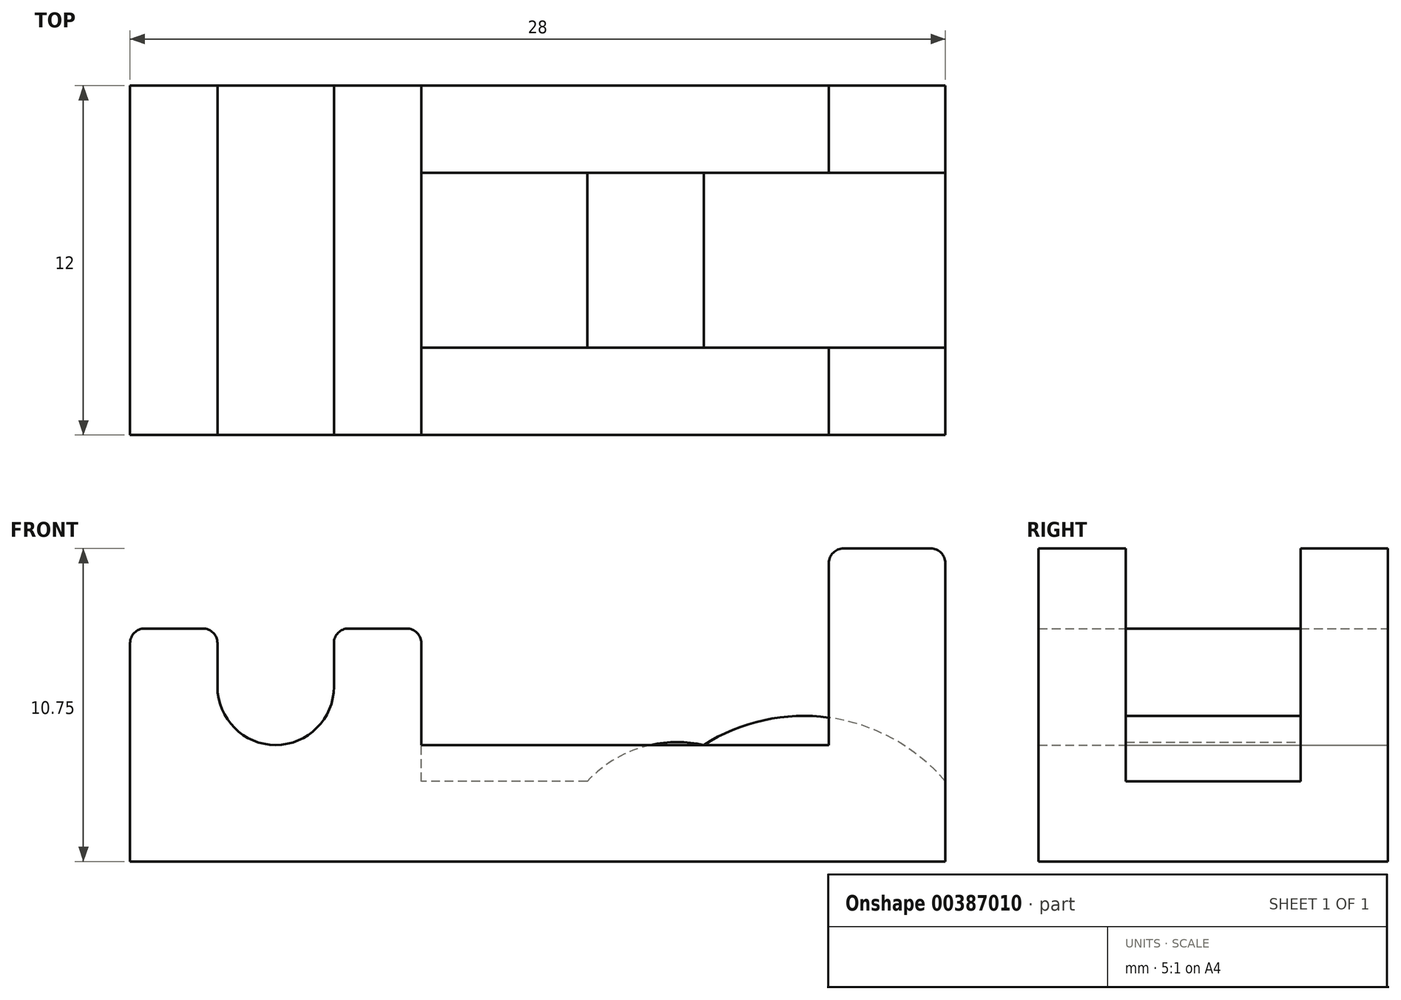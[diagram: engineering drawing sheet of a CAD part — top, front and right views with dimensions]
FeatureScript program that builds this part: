
annotation { "Feature Type Name" : "Feature", "Feature Type Description" : "" }
export const myFeature = defineFeature(function(context is Context, id is Id, definition is map)
    precondition{}
    {
        {
            var Q0;
            Q0=qCreatedBy(makeId("Front.planeOp"),FACE);
            var sketch = newSketch(context, id + "F0", { "sketchPlane" : qUnion([Q0])});
            skLineSegment(sketch, "E0", {"start": v(0, 0) * mm, "end": v(-28, 0) * mm});
            skLineSegment(sketch, "E1", {"start": v(0, 0) * mm, "end": v(0, 10.75) * mm});
            skLineSegment(sketch, "E2", {"start": v(0, 10.75) * mm, "end": v(-4, 10.75) * mm});
            skLineSegment(sketch, "E3", {"start": v(-4, 10.75) * mm, "end": v(-4, 4) * mm});
            skLineSegment(sketch, "E4", {"start": v(-4, 4) * mm, "end": v(-18, 4) * mm});
            skLineSegment(sketch, "E5", {"start": v(-28, 0) * mm, "end": v(-28, 8) * mm});
            skLineSegment(sketch, "E6", {"start": v(-25, 8) * mm, "end": v(-25, 6) * mm});
            skLineSegment(sketch, "E7", {"start": v(-21, 6) * mm, "end": v(-21, 8) * mm});
            skLineSegment(sketch, "E8", {"start": v(-18, 4) * mm, "end": v(-18, 8) * mm});
            skArc(sketch, "E9", {"start": v(-25, 6) * mm, "mid": v(-23, 4) * mm, "end": v(-21, 6) * mm});
            skLineSegment(sketch, "E10", {"start": v(-25, 8) * mm, "end": v(-28, 8) * mm});
            skLineSegment(sketch, "E11", {"start": v(-18, 8) * mm, "end": v(-21, 8) * mm});
            skSolve(sketch);
        }
        {
            var Q0;
            Q0=makeQuery(id+"F0.imprint","IMPRINT",FACE,{"disambiguationData":[TD([[makeQuery(id+"F0.imprint","IMPRINT",EDGE,{"derivedFrom":sQuery(id+"F0.wireOp",EDGE,"E0")}),-1.0]])]});
            extrude(context, id + "F1", {"entities" : qUnion([Q0]), "endBound" : BoundingType.SYMMETRIC, "depth" : 12 * mm});
        }
        {
            var Q0;
            Q0=makeQuery(id+"F1.opExtrude","SWEPT_FACE",FACE,{"disambiguationData":[OSD([sQuery(id+"F0.wireOp",EDGE,"E2")])]});
            var sketch = newSketch(context, id + "F2", { "sketchPlane" : qUnion([Q0])});
            skLineSegment(sketch, "E12.0", {"start": v(0, -6) * mm, "end": v(0, 6) * mm, "construction": true});
            skLineSegment(sketch, "E13.0", {"start": v(-18, -6) * mm, "end": v(-18, 6) * mm, "construction": true});
            skLineSegment(sketch, "E14.bottom", {"start": v(0, 3) * mm, "end": v(-18, 3) * mm});
            skLineSegment(sketch, "E14.top", {"start": v(0, -3) * mm, "end": v(-18, -3) * mm});
            skLineSegment(sketch, "E14.left", {"start": v(0, 3) * mm, "end": v(0, -3) * mm});
            skLineSegment(sketch, "E14.right", {"start": v(-18, 3) * mm, "end": v(-18, -3) * mm});
            skSolve(sketch);
        }
        {
            var Q0;
            {var subQ0=sQuery(id+"F2.wireOp",EDGE,"E14.right");Q0=makeQuery(id+"F2.imprint","IMPRINT",FACE,{"disambiguationData":[TD([[makeQuery(id+"F2.imprint","IMPRINT",EDGE,{"derivedFrom":subQ0}),1.0]])]});}
            var Q1;
            {var subQ0=sQuery(id+"F2.wireOp",EDGE,"E14.left");Q1=makeQuery(id+"F2.imprint","IMPRINT",FACE,{"disambiguationData":[TD([[makeQuery(id+"F2.imprint","IMPRINT",EDGE,{"derivedFrom":subQ0}),1.0]])]});}
            extrude(context, id + "F3", {"entities" : qUnion([Q0, Q1]), "operationType" : NewBodyOperationType.REMOVE, "oppositeDirection" : true, "depth" : 8 * mm});
        }
        {
            var Q0;
            Q0=qCreatedBy(makeId("Front.planeOp"),FACE);
            var sketch = newSketch(context, id + "F4", { "sketchPlane" : qUnion([Q0])});
            skLineSegment(sketch, "E15.0", {"start": v(0, 2.75) * mm, "end": v(-18, 2.75) * mm});
            skArc(sketch, "E16", {"start": v(0, 2.75) * mm, "mid": v(-3.92, 4.93) * mm, "end": v(-8.3, 4) * mm});
            skLineSegment(sketch, "E17", {"start": v(-16.7, 5) * mm, "end": v(1.87, 5) * mm, "construction": true});
            skArc(sketch, "E18", {"start": v(-8.3, 4) * mm, "mid": v(-10.47, 3.9) * mm, "end": v(-12.3, 2.75) * mm});
            skLineSegment(sketch, "E19.0", {"start": v(-4, 4) * mm, "end": v(-18, 4) * mm, "construction": true});
            skLineSegment(sketch, "E20", {"start": v(-12.3, 2.75) * mm, "end": v(0, 2.75) * mm});
            skSolve(sketch);
        }
        {
            var Q0;
            Q0=makeQuery(id+"F4.imprint","IMPRINT",FACE,{"disambiguationData":[TD([[makeQuery(id+"F4.imprint","IMPRINT",EDGE,{"derivedFrom":sQuery(id+"F4.wireOp",EDGE,"E16")}),1.0]])]});
            extrude(context, id + "F5", {"entities" : qUnion([Q0]), "operationType" : NewBodyOperationType.ADD, "endBound" : BoundingType.SYMMETRIC, "depth" : 6 * mm});
        }
        {
            var Q0;
            Q0=makeQuery(id+"F1.opExtrude","SWEPT_EDGE",EDGE,{"disambiguationData":[OSD([sQuery(id+"F0.wireOp",EDGE,"E7"),sQuery(id+"F0.wireOp",EDGE,"E11")])]});
            var Q1;
            Q1=makeQuery(id+"F1.opExtrude","SWEPT_EDGE",EDGE,{"disambiguationData":[OSD([sQuery(id+"F0.wireOp",EDGE,"E6"),sQuery(id+"F0.wireOp",EDGE,"E10")])]});
            var Q2;
            Q2=makeQuery(id+"F1.opExtrude","SWEPT_EDGE",EDGE,{"disambiguationData":[OSD([sQuery(id+"F0.wireOp",EDGE,"E5"),sQuery(id+"F0.wireOp",EDGE,"E10")])]});
            var Q3;
            Q3=makeQuery(id+"F1.opExtrude","SWEPT_EDGE",EDGE,{"disambiguationData":[OSD([sQuery(id+"F0.wireOp",EDGE,"E8"),sQuery(id+"F0.wireOp",EDGE,"E11")])]});
            var Q4;
            {var subQ0=sQuery(id+"F0.wireOp",EDGE,"E2");var subQ1=sQuery(id+"F0.wireOp",EDGE,"E1");Q4=makeQuery(id+"F3.boolean.opBoolean","SPLIT",EDGE,{"disambiguationData":[TD([makeQuery(id+"F3.opExtrude","SWEPT_FACE",FACE,{"disambiguationData":[OSD([sQuery(id+"F2.wireOp",EDGE,"E14.top")])]})])],"derivedFrom":makeQuery(id+"F1.opExtrude","SWEPT_EDGE",EDGE,{"disambiguationData":[OSD([subQ1,subQ0])]})});}
            var Q5;
            {var subQ0=sQuery(id+"F0.wireOp",EDGE,"E3");var subQ1=sQuery(id+"F0.wireOp",EDGE,"E2");Q5=makeQuery(id+"F3.boolean.opBoolean","SPLIT",EDGE,{"disambiguationData":[TD([makeQuery(id+"F3.opExtrude","SWEPT_FACE",FACE,{"disambiguationData":[OSD([sQuery(id+"F2.wireOp",EDGE,"E14.top")])]})])],"derivedFrom":makeQuery(id+"F1.opExtrude","SWEPT_EDGE",EDGE,{"disambiguationData":[OSD([subQ1,subQ0])]})});}
            var Q6;
            {var subQ0=sQuery(id+"F0.wireOp",EDGE,"E2");var subQ1=sQuery(id+"F0.wireOp",EDGE,"E1");Q6=makeQuery(id+"F3.boolean.opBoolean","SPLIT",EDGE,{"disambiguationData":[TD([makeQuery(id+"F3.opExtrude","SWEPT_FACE",FACE,{"disambiguationData":[OSD([sQuery(id+"F2.wireOp",EDGE,"E14.bottom")])]})])],"derivedFrom":makeQuery(id+"F1.opExtrude","SWEPT_EDGE",EDGE,{"disambiguationData":[OSD([subQ1,subQ0])]})});}
            var Q7;
            {var subQ0=sQuery(id+"F0.wireOp",EDGE,"E3");var subQ1=sQuery(id+"F0.wireOp",EDGE,"E2");Q7=makeQuery(id+"F3.boolean.opBoolean","SPLIT",EDGE,{"disambiguationData":[TD([makeQuery(id+"F3.opExtrude","SWEPT_FACE",FACE,{"disambiguationData":[OSD([sQuery(id+"F2.wireOp",EDGE,"E14.bottom")])]})])],"derivedFrom":makeQuery(id+"F1.opExtrude","SWEPT_EDGE",EDGE,{"disambiguationData":[OSD([subQ1,subQ0])]})});}
            fillet(context, id + "F6", {"entities" : qUnion([Q0, Q1, Q2, Q3, Q4, Q5, Q6, Q7]), "radius" : 0.5 * mm, "tangentPropagation" : true, "allowEdgeOverflow" : false});
        }
    });
